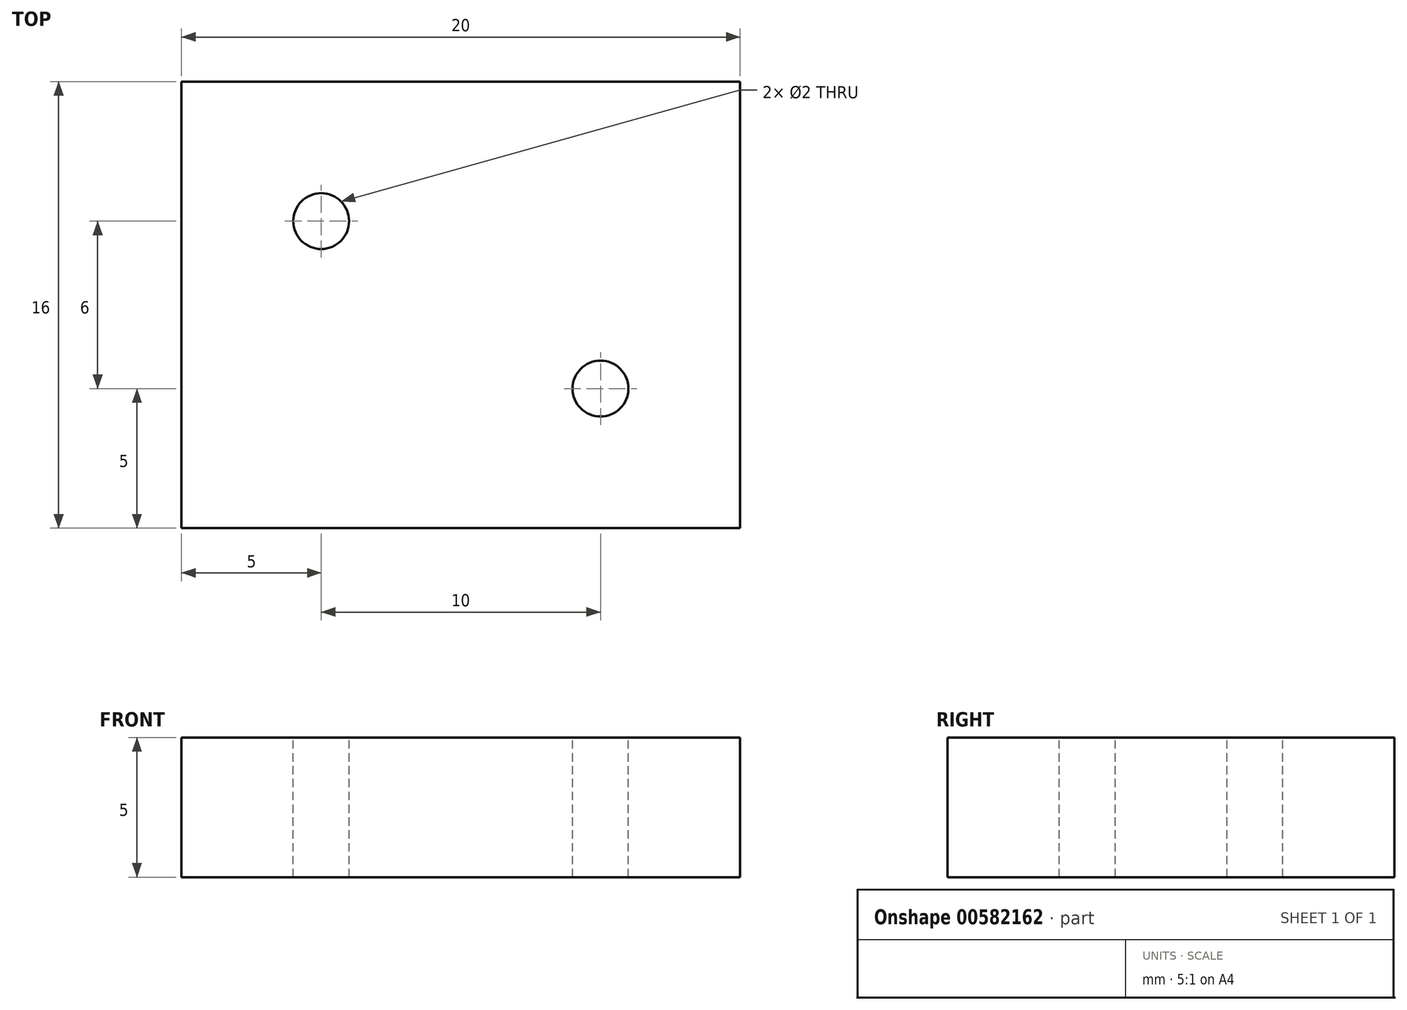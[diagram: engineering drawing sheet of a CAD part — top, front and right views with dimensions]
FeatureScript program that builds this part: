
annotation { "Feature Type Name" : "Feature", "Feature Type Description" : "" }
export const myFeature = defineFeature(function(context is Context, id is Id, definition is map)
    precondition{}
    {
        {
            var Q0;
            Q0=qCreatedBy(makeId("Top.planeOp"),FACE);
            var sketch = newSketch(context, id + "F0", { "sketchPlane" : qUnion([Q0])});
            skLineSegment(sketch, "E0.bottom", {"start": v(10, -8) * mm, "end": v(-10, -8) * mm});
            skLineSegment(sketch, "E0.top", {"start": v(10, 8) * mm, "end": v(-10, 8) * mm});
            skLineSegment(sketch, "E0.left", {"start": v(10, -8) * mm, "end": v(10, 8) * mm});
            skLineSegment(sketch, "E0.right", {"start": v(-10, -8) * mm, "end": v(-10, 8) * mm});
            skPoint(sketch, "E0.middle", {"position": v(0, 0) * mm});
            skSolve(sketch);
        }
        {
            var Q0;
            Q0 = qSketchRegion(id + "F0", true);
            extrude(context, id + "F1", {"entities" : qUnion([Q0]), "depth" : 5 * mm, "offsetDistance" : 25 * mm});
        }
        {
            var Q0;
            Q0=makeQuery(id+"F1.opExtrude","CAP_FACE",FACE,{"disambiguationData":[OSD([sQuery(id+"F0.wireOp",EDGE,"E0.bottom"),sQuery(id+"F0.wireOp",EDGE,"E0.top"),sQuery(id+"F0.wireOp",EDGE,"E0.left"),sQuery(id+"F0.wireOp",EDGE,"E0.right")])],"isStart":false});
            var sketch = newSketch(context, id + "F2", { "sketchPlane" : qUnion([Q0])});
            skCircle(sketch, "E1", {"center": v(-5, 3) * mm, "radius": 1 * mm});
            skCircle(sketch, "E2", {"center": v(5, -3) * mm, "radius": 1 * mm});
            skSolve(sketch);
        }
        {
            var Q0;
            Q0=makeQuery(id+"F2.imprint","IMPRINT",FACE,{"disambiguationData":[TD([[makeQuery(id+"F2.imprint","IMPRINT",EDGE,{"derivedFrom":sQuery(id+"F2.wireOp",EDGE,"E2")}),1.0]])]});
            var Q1;
            Q1=makeQuery(id+"F2.imprint","IMPRINT",FACE,{"disambiguationData":[TD([[makeQuery(id+"F2.imprint","IMPRINT",EDGE,{"derivedFrom":sQuery(id+"F2.wireOp",EDGE,"E1")}),1.0]])]});
            extrude(context, id + "F3", {"entities" : qUnion([Q0, Q1]), "operationType" : NewBodyOperationType.REMOVE, "oppositeDirection" : true, "depth" : 25 * mm, "offsetDistance" : 25 * mm});
        }
    });
